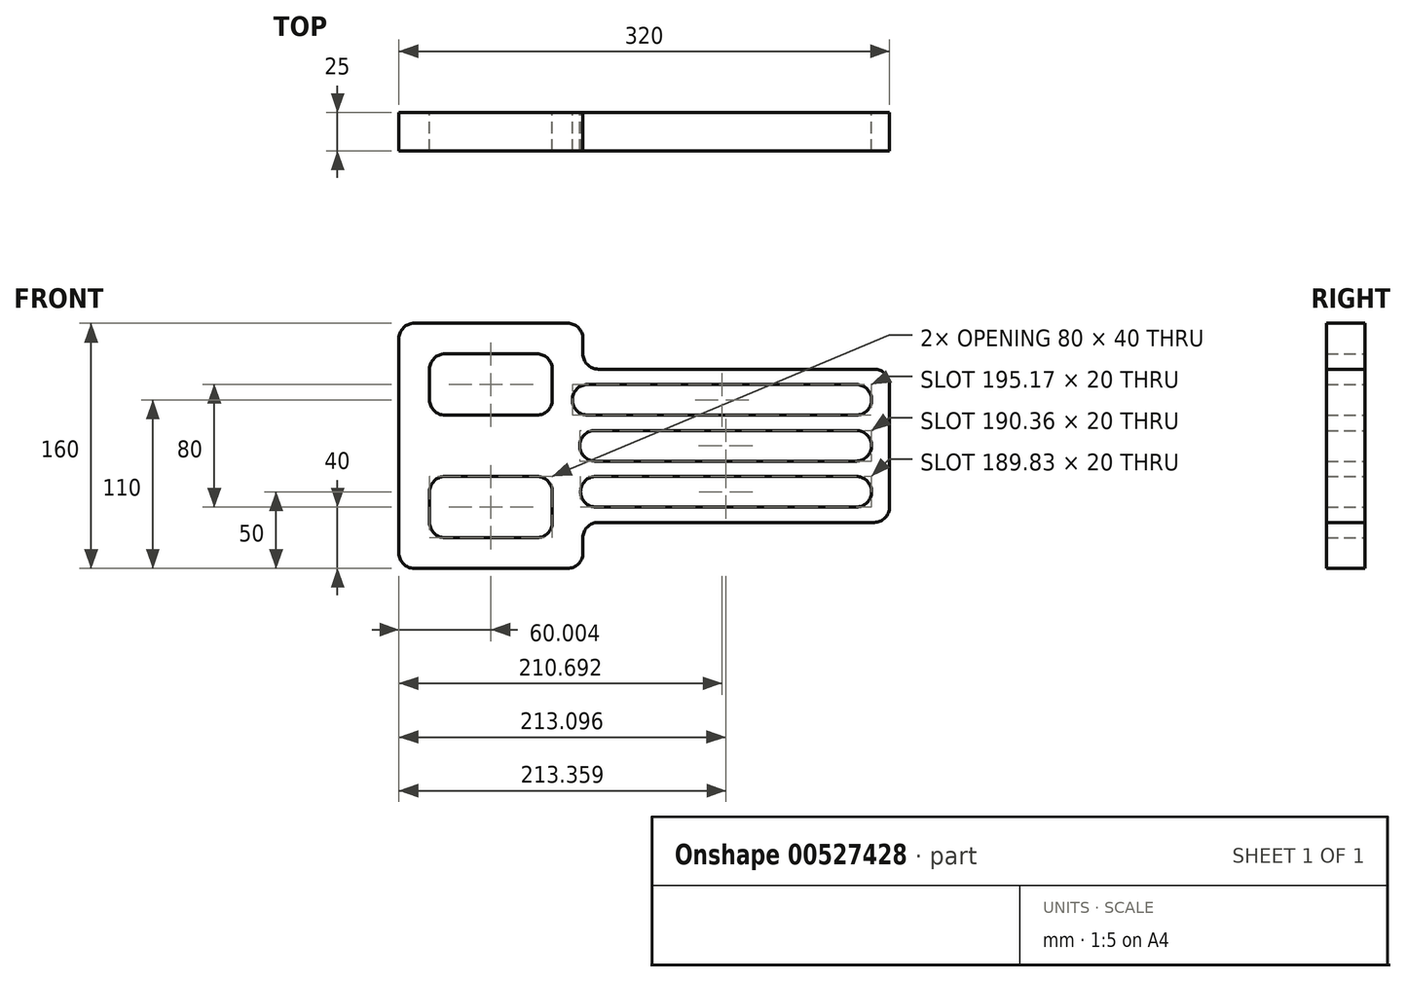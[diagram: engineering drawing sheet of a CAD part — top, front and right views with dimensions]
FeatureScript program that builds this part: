
annotation { "Feature Type Name" : "Feature", "Feature Type Description" : "" }
export const myFeature = defineFeature(function(context is Context, id is Id, definition is map)
    precondition{}
    {
        {
            var Q0;
            Q0=qCreatedBy(makeId("Front.planeOp"),FACE);
            var sketch = newSketch(context, id + "F0", { "sketchPlane" : qUnion([Q0])});
            skLineSegment(sketch, "E0", {"start": v(-99.15, 70.14) * mm, "end": v(-99.15, -69.86) * mm});
            skLineSegment(sketch, "E1", {"start": v(-89.15, -79.86) * mm, "end": v(10.85, -79.86) * mm});
            skLineSegment(sketch, "E2", {"start": v(-89.15, 80.14) * mm, "end": v(10.85, 80.14) * mm});
            skLineSegment(sketch, "E3", {"start": v(20.85, 70.14) * mm, "end": v(20.85, 60.14) * mm});
            skLineSegment(sketch, "E4", {"start": v(20.85, -69.86) * mm, "end": v(20.85, -59.86) * mm});
            skLineSegment(sketch, "E5", {"start": v(30.85, 50.14) * mm, "end": v(210.85, 50.14) * mm});
            skLineSegment(sketch, "E6", {"start": v(30.85, -49.86) * mm, "end": v(210.85, -49.86) * mm});
            skLineSegment(sketch, "E7", {"start": v(220.85, 40.14) * mm, "end": v(220.85, -39.86) * mm});
            skLineSegment(sketch, "E8.bottom", {"start": v(199.13, 40.14) * mm, "end": v(23.96, 40.14) * mm});
            skLineSegment(sketch, "E8.top", {"start": v(199.13, 20.14) * mm, "end": v(23.96, 20.14) * mm});
            skLineSegment(sketch, "E8.left", {"start": v(209.13, 30.14) * mm, "end": v(209.13, 30.14) * mm});
            skLineSegment(sketch, "E8.right", {"start": v(13.96, 30.14) * mm, "end": v(13.96, 30.14) * mm});
            skLineSegment(sketch, "E9.bottom", {"start": v(28.77, 10.14) * mm, "end": v(199.13, 10.14) * mm});
            skLineSegment(sketch, "E9.top", {"start": v(28.77, -9.86) * mm, "end": v(199.13, -9.86) * mm});
            skLineSegment(sketch, "E9.left", {"start": v(18.77, 0.14) * mm, "end": v(18.77, 0.14) * mm});
            skLineSegment(sketch, "E10.bottom", {"start": v(29.3, -19.86) * mm, "end": v(199.13, -19.86) * mm});
            skLineSegment(sketch, "E10.top", {"start": v(29.3, -39.86) * mm, "end": v(199.13, -39.86) * mm});
            skLineSegment(sketch, "E10.left", {"start": v(19.3, -29.86) * mm, "end": v(19.3, -29.86) * mm});
            skLineSegment(sketch, "E10.right", {"start": v(209.13, -29.86) * mm, "end": v(209.13, -29.86) * mm});
            skLineSegment(sketch, "E11", {"start": v(208.97, 40.14) * mm, "end": v(208.8, 20.14) * mm});
            skPoint(sketch, "E12.orphan", {"position": v(209.13, -49.86) * mm});
            skLineSegment(sketch, "E13", {"start": v(209.13, 0.14) * mm, "end": v(209.13, 0.14) * mm});
            skLineSegment(sketch, "E14.bottom", {"start": v(-69.15, -19.86) * mm, "end": v(-9.15, -19.86) * mm});
            skLineSegment(sketch, "E14.top", {"start": v(-69.15, -59.86) * mm, "end": v(-9.15, -59.86) * mm});
            skLineSegment(sketch, "E14.left", {"start": v(-79.15, -29.86) * mm, "end": v(-79.15, -49.86) * mm});
            skLineSegment(sketch, "E14.right", {"start": v(0.85, -29.86) * mm, "end": v(0.85, -49.86) * mm});
            skLineSegment(sketch, "E15.bottom", {"start": v(-69.15, 60.14) * mm, "end": v(-9.15, 60.14) * mm});
            skLineSegment(sketch, "E15.top", {"start": v(-69.15, 20.14) * mm, "end": v(-9.15, 20.14) * mm});
            skLineSegment(sketch, "E15.left", {"start": v(-79.15, 50.14) * mm, "end": v(-79.15, 30.14) * mm});
            skLineSegment(sketch, "E15.right", {"start": v(0.85, 50.14) * mm, "end": v(0.85, 30.14) * mm});
            skPoint(sketch, "E16.start.orphan", {"position": v(-39.15, -79.86) * mm});
            skPoint(sketch, "E17.visualSharp", {"position": v(13.96, 40.14) * mm});
            skArc(sketch, "E17.filletArc", {"start": v(23.96, 40.14) * mm, "mid": v(16.89, 37.21) * mm, "end": v(13.96, 30.14) * mm});
            skPoint(sketch, "E18.visualSharp", {"position": v(13.96, 20.14) * mm});
            skArc(sketch, "E18.filletArc", {"start": v(13.96, 30.14) * mm, "mid": v(16.89, 23.07) * mm, "end": v(23.96, 20.14) * mm});
            skPoint(sketch, "E19.visualSharp", {"position": v(209.13, 40.14) * mm});
            skArc(sketch, "E19.filletArc", {"start": v(209.13, 30.14) * mm, "mid": v(206.2, 37.21) * mm, "end": v(199.13, 40.14) * mm});
            skPoint(sketch, "E20.visualSharp", {"position": v(209.13, 20.14) * mm});
            skArc(sketch, "E20.filletArc", {"start": v(199.13, 20.14) * mm, "mid": v(206.2, 23.07) * mm, "end": v(209.13, 30.14) * mm});
            skPoint(sketch, "E21.visualSharp", {"position": v(209.13, 10.14) * mm});
            skArc(sketch, "E21.filletArc", {"start": v(209.13, 0.14) * mm, "mid": v(206.2, 7.21) * mm, "end": v(199.13, 10.14) * mm});
            skPoint(sketch, "E22.visualSharp", {"position": v(209.13, -9.86) * mm});
            skArc(sketch, "E22.filletArc", {"start": v(199.13, -9.86) * mm, "mid": v(206.2, -6.93) * mm, "end": v(209.13, 0.14) * mm});
            skPoint(sketch, "E23.visualSharp", {"position": v(18.77, -9.86) * mm});
            skArc(sketch, "E23.filletArc", {"start": v(18.77, 0.14) * mm, "mid": v(21.7, -6.93) * mm, "end": v(28.77, -9.86) * mm});
            skPoint(sketch, "E24.visualSharp", {"position": v(18.77, 10.14) * mm});
            skArc(sketch, "E24.filletArc", {"start": v(28.77, 10.14) * mm, "mid": v(21.7, 7.21) * mm, "end": v(18.77, 0.14) * mm});
            skPoint(sketch, "E25.visualSharp", {"position": v(19.3, -19.86) * mm});
            skArc(sketch, "E25.filletArc", {"start": v(29.3, -19.86) * mm, "mid": v(22.22, -22.79) * mm, "end": v(19.3, -29.86) * mm});
            skPoint(sketch, "E26.visualSharp", {"position": v(19.3, -39.86) * mm});
            skArc(sketch, "E26.filletArc", {"start": v(19.3, -29.86) * mm, "mid": v(22.22, -36.93) * mm, "end": v(29.3, -39.86) * mm});
            skPoint(sketch, "E27.visualSharp", {"position": v(209.13, -19.86) * mm});
            skArc(sketch, "E27.filletArc", {"start": v(209.13, -29.86) * mm, "mid": v(206.2, -22.79) * mm, "end": v(199.13, -19.86) * mm});
            skPoint(sketch, "E28.visualSharp", {"position": v(209.13, -39.86) * mm});
            skArc(sketch, "E28.filletArc", {"start": v(199.13, -39.86) * mm, "mid": v(206.2, -36.93) * mm, "end": v(209.13, -29.86) * mm});
            skPoint(sketch, "E29.visualSharp", {"position": v(220.85, 50.14) * mm});
            skArc(sketch, "E29.filletArc", {"start": v(220.85, 40.14) * mm, "mid": v(217.93, 47.21) * mm, "end": v(210.85, 50.14) * mm});
            skPoint(sketch, "E30.visualSharp", {"position": v(220.85, -49.86) * mm});
            skArc(sketch, "E30.filletArc", {"start": v(210.85, -49.86) * mm, "mid": v(217.93, -46.93) * mm, "end": v(220.85, -39.86) * mm});
            skPoint(sketch, "E31.visualSharp", {"position": v(20.85, -79.86) * mm});
            skArc(sketch, "E31.filletArc", {"start": v(10.85, -79.86) * mm, "mid": v(17.93, -76.93) * mm, "end": v(20.85, -69.86) * mm});
            skPoint(sketch, "E32.visualSharp", {"position": v(-99.15, -79.86) * mm});
            skArc(sketch, "E32.filletArc", {"start": v(-99.15, -69.86) * mm, "mid": v(-96.22, -76.93) * mm, "end": v(-89.15, -79.86) * mm});
            skPoint(sketch, "E33.visualSharp", {"position": v(-99.15, 80.14) * mm});
            skArc(sketch, "E33.filletArc", {"start": v(-89.15, 80.14) * mm, "mid": v(-96.22, 77.21) * mm, "end": v(-99.15, 70.14) * mm});
            skPoint(sketch, "E34.visualSharp", {"position": v(20.85, 80.14) * mm});
            skArc(sketch, "E34.filletArc", {"start": v(20.85, 70.14) * mm, "mid": v(17.93, 77.21) * mm, "end": v(10.85, 80.14) * mm});
            skPoint(sketch, "E35.visualSharp", {"position": v(20.85, -49.86) * mm});
            skArc(sketch, "E35.filletArc", {"start": v(30.85, -49.86) * mm, "mid": v(23.78, -52.79) * mm, "end": v(20.85, -59.86) * mm});
            skPoint(sketch, "E36.visualSharp", {"position": v(20.85, 50.14) * mm});
            skArc(sketch, "E36.filletArc", {"start": v(20.85, 60.14) * mm, "mid": v(23.78, 53.07) * mm, "end": v(30.85, 50.14) * mm});
            skPoint(sketch, "E37.visualSharp", {"position": v(0.85, 20.14) * mm});
            skArc(sketch, "E37.filletArc", {"start": v(-9.15, 20.14) * mm, "mid": v(-2.07, 23.07) * mm, "end": v(0.85, 30.14) * mm});
            skPoint(sketch, "E38.visualSharp", {"position": v(0.85, 60.14) * mm});
            skArc(sketch, "E38.filletArc", {"start": v(0.85, 50.14) * mm, "mid": v(-2.07, 57.21) * mm, "end": v(-9.15, 60.14) * mm});
            skPoint(sketch, "E39.visualSharp", {"position": v(-79.15, 60.14) * mm});
            skArc(sketch, "E39.filletArc", {"start": v(-69.15, 60.14) * mm, "mid": v(-76.22, 57.21) * mm, "end": v(-79.15, 50.14) * mm});
            skPoint(sketch, "E40.visualSharp", {"position": v(-79.15, 20.14) * mm});
            skArc(sketch, "E40.filletArc", {"start": v(-79.15, 30.14) * mm, "mid": v(-76.22, 23.07) * mm, "end": v(-69.15, 20.14) * mm});
            skPoint(sketch, "E41.visualSharp", {"position": v(-79.15, -19.86) * mm});
            skArc(sketch, "E41.filletArc", {"start": v(-69.15, -19.86) * mm, "mid": v(-76.22, -22.79) * mm, "end": v(-79.15, -29.86) * mm});
            skPoint(sketch, "E42.visualSharp", {"position": v(0.85, -19.86) * mm});
            skArc(sketch, "E42.filletArc", {"start": v(0.85, -29.86) * mm, "mid": v(-2.07, -22.79) * mm, "end": v(-9.15, -19.86) * mm});
            skPoint(sketch, "E43.visualSharp", {"position": v(-79.15, -59.86) * mm});
            skArc(sketch, "E43.filletArc", {"start": v(-79.15, -49.86) * mm, "mid": v(-76.22, -56.93) * mm, "end": v(-69.15, -59.86) * mm});
            skPoint(sketch, "E44.visualSharp", {"position": v(0.85, -59.86) * mm});
            skArc(sketch, "E44.filletArc", {"start": v(-9.15, -59.86) * mm, "mid": v(-2.07, -56.93) * mm, "end": v(0.85, -49.86) * mm});
            skSolve(sketch);
        }
        {
            var Q0;
            Q0 = qSketchRegion(id + "F0", true);
            extrude(context, id + "F1", {"entities" : qUnion([Q0]), "depth" : 25 * mm, "offsetDistance" : 25 * mm});
        }
    });
